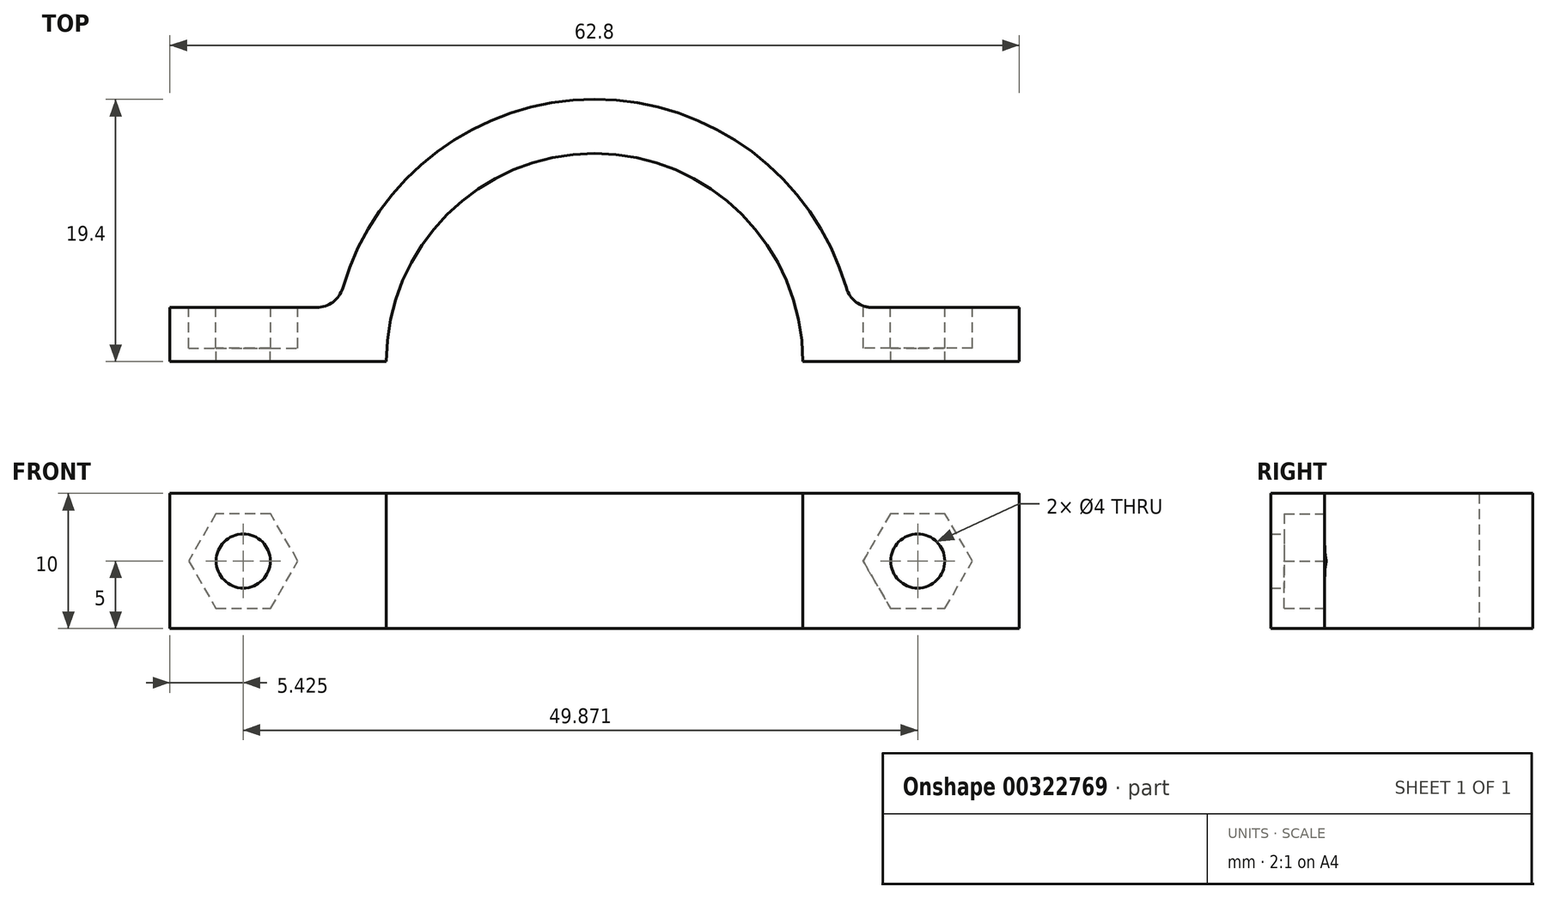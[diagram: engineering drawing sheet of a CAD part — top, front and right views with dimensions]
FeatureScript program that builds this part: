
annotation { "Feature Type Name" : "Feature", "Feature Type Description" : "" }
export const myFeature = defineFeature(function(context is Context, id is Id, definition is map)
    precondition{}
    {
        {
            var Q0;
            Q0=qCreatedBy(makeId("Top.planeOp"),FACE);
            var sketch = newSketch(context, id + "F0", { "sketchPlane" : qUnion([Q0])});
            skArc(sketch, "E0", {"start": v(-27.8, -38.88) * mm, "mid": v(-43.2, -23.48) * mm, "end": v(-58.6, -38.88) * mm});
            skArc(sketch, "E1.0", {"start": v(-24.58, -33.44) * mm, "mid": v(-43.2, -19.48) * mm, "end": v(-61.83, -33.44) * mm});
            skLineSegment(sketch, "E2", {"start": v(-62.6, -38.88) * mm, "end": v(-58.6, -38.88) * mm});
            skLineSegment(sketch, "E3", {"start": v(-62.6, -38.88) * mm, "end": v(-74.6, -38.88) * mm});
            skLineSegment(sketch, "E4", {"start": v(-74.6, -38.88) * mm, "end": v(-74.6, -34.88) * mm});
            skLineSegment(sketch, "E5", {"start": v(-74.6, -34.88) * mm, "end": v(-63.75, -34.88) * mm});
            skLineSegment(sketch, "E6", {"start": v(71.2, 95.03) * mm, "end": v(72.93, 94.03) * mm});
            skLineSegment(sketch, "E7", {"start": v(72.93, 94.03) * mm, "end": v(75.53, 92.53) * mm});
            skPoint(sketch, "E8.visualSharp", {"position": v(-62.19, -34.88) * mm});
            skArc(sketch, "E8.filletArc", {"start": v(-63.75, -34.88) * mm, "mid": v(-62.55, -34.48) * mm, "end": v(-61.83, -33.44) * mm});
            skLineSegment(sketch, "E9", {"start": v(-22.66, -34.88) * mm, "end": v(-11.8, -34.88) * mm});
            skLineSegment(sketch, "E10", {"start": v(-27.8, -38.88) * mm, "end": v(-11.8, -38.88) * mm});
            skLineSegment(sketch, "E11", {"start": v(-11.8, -38.88) * mm, "end": v(-11.8, -34.88) * mm});
            skPoint(sketch, "E12.visualSharp", {"position": v(-24.22, -34.88) * mm});
            skArc(sketch, "E12.filletArc", {"start": v(-24.58, -33.44) * mm, "mid": v(-23.86, -34.48) * mm, "end": v(-22.66, -34.88) * mm});
            skSolve(sketch);
        }
        {
            var Q0;
            Q0=makeQuery(id+"F0.imprint","IMPRINT",FACE,{"disambiguationData":[TD([[makeQuery(id+"F0.imprint","IMPRINT",EDGE,{"derivedFrom":sQuery(id+"F0.wireOp",EDGE,"E0")}),-1.0]])]});
            extrude(context, id + "F1", {"entities" : qUnion([Q0]), "depth" : 10 * mm});
        }
        {
            var Q0;
            Q0=makeQuery(id+"F1.opExtrude","SWEPT_FACE",FACE,{"disambiguationData":[OSD([sQuery(id+"F0.wireOp",EDGE,"E5")])]});
            var sketch = newSketch(context, id + "F2", { "sketchPlane" : qUnion([Q0])});
            skCircle(sketch, "E13", {"center": v(69.17, 5) * mm, "radius": 2 * mm});
            skCircle(sketch, "E14", {"center": v(19.3, 5) * mm, "radius": 2 * mm});
            skSolve(sketch);
        }
        {
            var Q0;
            Q0 = qSketchRegion(id + "F2", true);
            extrude(context, id + "F3", {"entities" : qUnion([Q0]), "operationType" : NewBodyOperationType.REMOVE, "endBound" : BoundingType.THROUGH_ALL, "oppositeDirection" : true, "depth" : 25 * mm});
        }
        {
            var Q0;
            Q0=makeQuery(id+"F1.opExtrude","SWEPT_FACE",FACE,{"disambiguationData":[OSD([sQuery(id+"F0.wireOp",EDGE,"E5")])]});
            var sketch = newSketch(context, id + "F4", { "sketchPlane" : qUnion([Q0])});
            skCircle(sketch, "E15.cCircle", {"center": v(69.17, 5) * mm, "radius": 4.04 * mm, "construction": true});
            skLineSegment(sketch, "E15.0", {"start": v(67.15, 1.5) * mm, "end": v(65.13, 5) * mm});
            skLineSegment(sketch, "E15.1", {"start": v(65.13, 5) * mm, "end": v(67.15, 8.5) * mm});
            skLineSegment(sketch, "E15.2", {"start": v(67.15, 8.5) * mm, "end": v(71.2, 8.5) * mm});
            skLineSegment(sketch, "E15.3", {"start": v(71.2, 8.5) * mm, "end": v(73.22, 5) * mm});
            skLineSegment(sketch, "E15.4", {"start": v(73.22, 5) * mm, "end": v(71.2, 1.5) * mm});
            skLineSegment(sketch, "E15.5", {"start": v(71.2, 1.5) * mm, "end": v(67.15, 1.5) * mm});
            skSolve(sketch);
        }
        {
            var Q0;
            Q0 = qSketchRegion(id + "F4", true);
            extrude(context, id + "F5", {"entities" : qUnion([Q0]), "operationType" : NewBodyOperationType.REMOVE, "oppositeDirection" : true, "depth" : 3 * mm});
        }
        {
            var Q0;
            Q0=makeQuery(id+"F1.opExtrude","SWEPT_FACE",FACE,{"disambiguationData":[OSD([sQuery(id+"F0.wireOp",EDGE,"E9")])]});
            var sketch = newSketch(context, id + "F6", { "sketchPlane" : qUnion([Q0])});
            skCircle(sketch, "E16.cCircle", {"center": v(19.3, 5) * mm, "radius": 4.04 * mm, "construction": true});
            skLineSegment(sketch, "E16.0", {"start": v(17.28, 1.5) * mm, "end": v(15.26, 5) * mm});
            skLineSegment(sketch, "E16.1", {"start": v(15.26, 5) * mm, "end": v(17.28, 8.5) * mm});
            skLineSegment(sketch, "E16.2", {"start": v(17.28, 8.5) * mm, "end": v(21.32, 8.5) * mm});
            skLineSegment(sketch, "E16.3", {"start": v(21.32, 8.5) * mm, "end": v(23.35, 5) * mm});
            skLineSegment(sketch, "E16.4", {"start": v(23.35, 5) * mm, "end": v(21.32, 1.5) * mm});
            skLineSegment(sketch, "E16.5", {"start": v(21.32, 1.5) * mm, "end": v(17.28, 1.5) * mm});
            skSolve(sketch);
        }
        {
            var Q0;
            Q0 = qSketchRegion(id + "F6", true);
            extrude(context, id + "F7", {"entities" : qUnion([Q0]), "operationType" : NewBodyOperationType.REMOVE, "oppositeDirection" : true, "depth" : 3 * mm});
        }
        {
            var Q0;
            Q0 = qSketchRegion(id + "F6", true);
            extrude(context, id + "F8", {"entities" : qUnion([Q0]), "operationType" : NewBodyOperationType.REMOVE, "depth" : 25 * mm});
        }
    });
